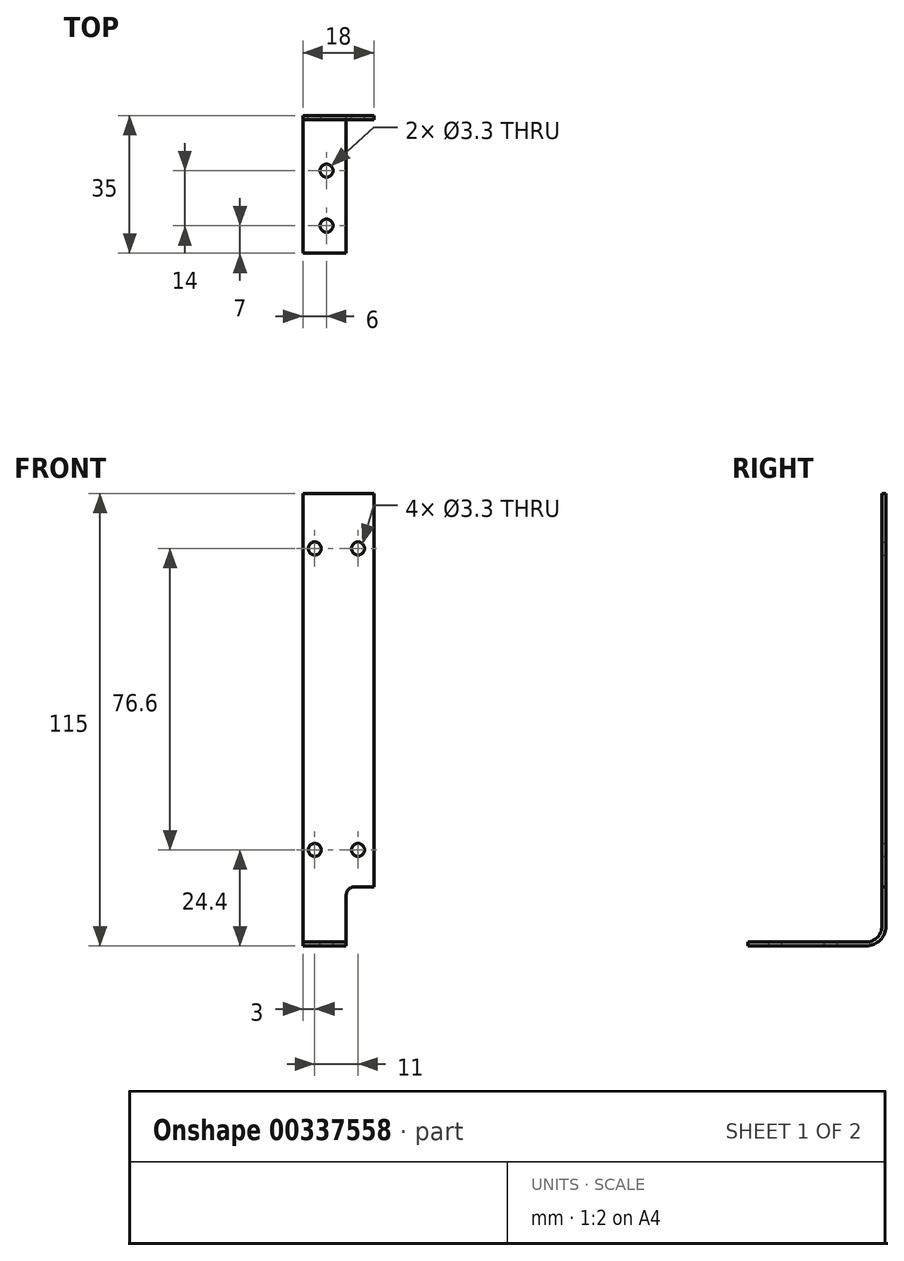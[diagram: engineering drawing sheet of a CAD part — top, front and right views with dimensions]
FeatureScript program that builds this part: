
annotation { "Feature Type Name" : "Feature", "Feature Type Description" : "" }
export const myFeature = defineFeature(function(context is Context, id is Id, definition is map)
    precondition{}
    {
        {
            var Q0;
            Q0=qCreatedBy(makeId("Right.planeOp"),FACE);
            var sketch = newSketch(context, id + "F0", { "sketchPlane" : qUnion([Q0])});
            skLineSegment(sketch, "E0", {"start": v(-5, 0) * mm, "end": v(-35, 0) * mm});
            skLineSegment(sketch, "E1", {"start": v(0, 5) * mm, "end": v(0, 115) * mm});
            skPoint(sketch, "E2.visualSharp", {"position": v(0, 0) * mm});
            skArc(sketch, "E2.filletArc", {"start": v(-5, 0) * mm, "mid": v(-1.46, 1.46) * mm, "end": v(0, 5) * mm});
            skSolve(sketch);
        }
        {
            var Q0;
            Q0=qCreatedBy(makeId("Front.planeOp"),FACE);
            var Q1;
            Q1=sQuery(id+"F0.wireOp",VERTEX,"E0.end");
            cPlane(context, id + "F1", {"entities" : qUnion([Q0, Q1]), "cplaneType" : CPlaneType.PLANE_POINT, "offset" : 25 * mm, "width" : 150 * mm, "height" : 150 * mm});
        }
        {
            var Q0;
            Q0=qCreatedBy(id+"F1.planeOp",FACE);
            var sketch = newSketch(context, id + "F2", { "sketchPlane" : qUnion([Q0])});
            skLineSegment(sketch, "E3.bottom", {"start": v(0, 0) * mm, "end": v(18, 0) * mm});
            skLineSegment(sketch, "E3.top", {"start": v(0, 1) * mm, "end": v(18, 1) * mm});
            skLineSegment(sketch, "E3.left", {"start": v(0, 0) * mm, "end": v(0, 1) * mm});
            skLineSegment(sketch, "E3.right", {"start": v(18, 0) * mm, "end": v(18, 1) * mm});
            skSolve(sketch);
        }
        {
            var Q0;
            Q0 = qSketchRegion(id + "F2", true);
            var Q1;
            Q1 = qConstructionFilter(qBodyType(qCreatedBy(id + "F0" ,EDGE), BodyType.WIRE), ConstructionObject.NO);
            sweep(context, id + "F3", {"profiles" : qUnion([Q0]), "path" : qUnion([Q1])});
        }
        {
            var Q0;
            Q0=makeQuery(id+"F3.opSweep","SWEPT_FACE",FACE,{"disambiguationData":[OSD([sQuery(id+"F0.wireOp",EDGE,"E0"),sQuery(id+"F2.wireOp",EDGE,"E3.top")])]});
            var sketch = newSketch(context, id + "F4", { "sketchPlane" : qUnion([Q0])});
            skCircle(sketch, "E4", {"center": v(6, -14) * mm, "radius": 1.65 * mm});
            skCircle(sketch, "E5", {"center": v(6, -28) * mm, "radius": 1.65 * mm});
            skLineSegment(sketch, "E6", {"start": v(6, -14) * mm, "end": v(6, -28) * mm, "construction": true});
            skSolve(sketch);
        }
        {
            var Q0;
            Q0 = qSketchRegion(id + "F4", true);
            extrude(context, id + "F5", {"entities" : qUnion([Q0]), "operationType" : NewBodyOperationType.REMOVE, "endBound" : BoundingType.UP_TO_NEXT, "oppositeDirection" : true, "depth" : 25 * mm});
        }
        {
            var Q0;
            Q0=makeQuery(id+"F3.opSweep","SWEPT_FACE",FACE,{"disambiguationData":[OSD([sQuery(id+"F0.wireOp",EDGE,"E1"),sQuery(id+"F2.wireOp",EDGE,"E3.bottom")])]});
            var sketch = newSketch(context, id + "F6", { "sketchPlane" : qUnion([Q0])});
            skCircle(sketch, "E7", {"center": v(-3, 24.4) * mm, "radius": 1.65 * mm});
            skCircle(sketch, "E8", {"center": v(-14, 24.4) * mm, "radius": 1.65 * mm});
            skCircle(sketch, "E9", {"center": v(-14, 101) * mm, "radius": 1.65 * mm});
            skCircle(sketch, "E10", {"center": v(-3, 101) * mm, "radius": 1.65 * mm});
            skLineSegment(sketch, "E11", {"start": v(-14, 24.4) * mm, "end": v(-3, 24.4) * mm, "construction": true});
            skLineSegment(sketch, "E12", {"start": v(-3, 101) * mm, "end": v(-3, 24.4) * mm, "construction": true});
            skLineSegment(sketch, "E13", {"start": v(-14, 101) * mm, "end": v(-14, 24.4) * mm, "construction": true});
            skLineSegment(sketch, "E14", {"start": v(-14, 101) * mm, "end": v(-3, 101) * mm, "construction": true});
            skLineSegment(sketch, "E15.0", {"start": v(-18, 0) * mm, "end": v(0, 0) * mm});
            skLineSegment(sketch, "E16.bottom", {"start": v(-18, 0) * mm, "end": v(-11, 0) * mm});
            skLineSegment(sketch, "E16.top", {"start": v(-18, 15) * mm, "end": v(-13, 15) * mm});
            skLineSegment(sketch, "E16.left", {"start": v(-18, 0) * mm, "end": v(-18, 15) * mm});
            skLineSegment(sketch, "E16.right", {"start": v(-11, 0) * mm, "end": v(-11, 13) * mm});
            skPoint(sketch, "E17.visualSharp", {"position": v(-11, 15) * mm});
            skArc(sketch, "E17.filletArc", {"start": v(-11, 13) * mm, "mid": v(-11.59, 14.41) * mm, "end": v(-13, 15) * mm});
            skPoint(sketch, "E18.0", {"position": v(-18, 115) * mm});
            skPoint(sketch, "E19.0", {"position": v(0, 115) * mm});
            skSolve(sketch);
        }
        {
            var Q0;
            Q0 = qSketchRegion(id + "F6", true);
            extrude(context, id + "F7", {"entities" : qUnion([Q0]), "operationType" : NewBodyOperationType.REMOVE, "endBound" : BoundingType.UP_TO_NEXT, "oppositeDirection" : true, "depth" : 25 * mm});
        }
    });
